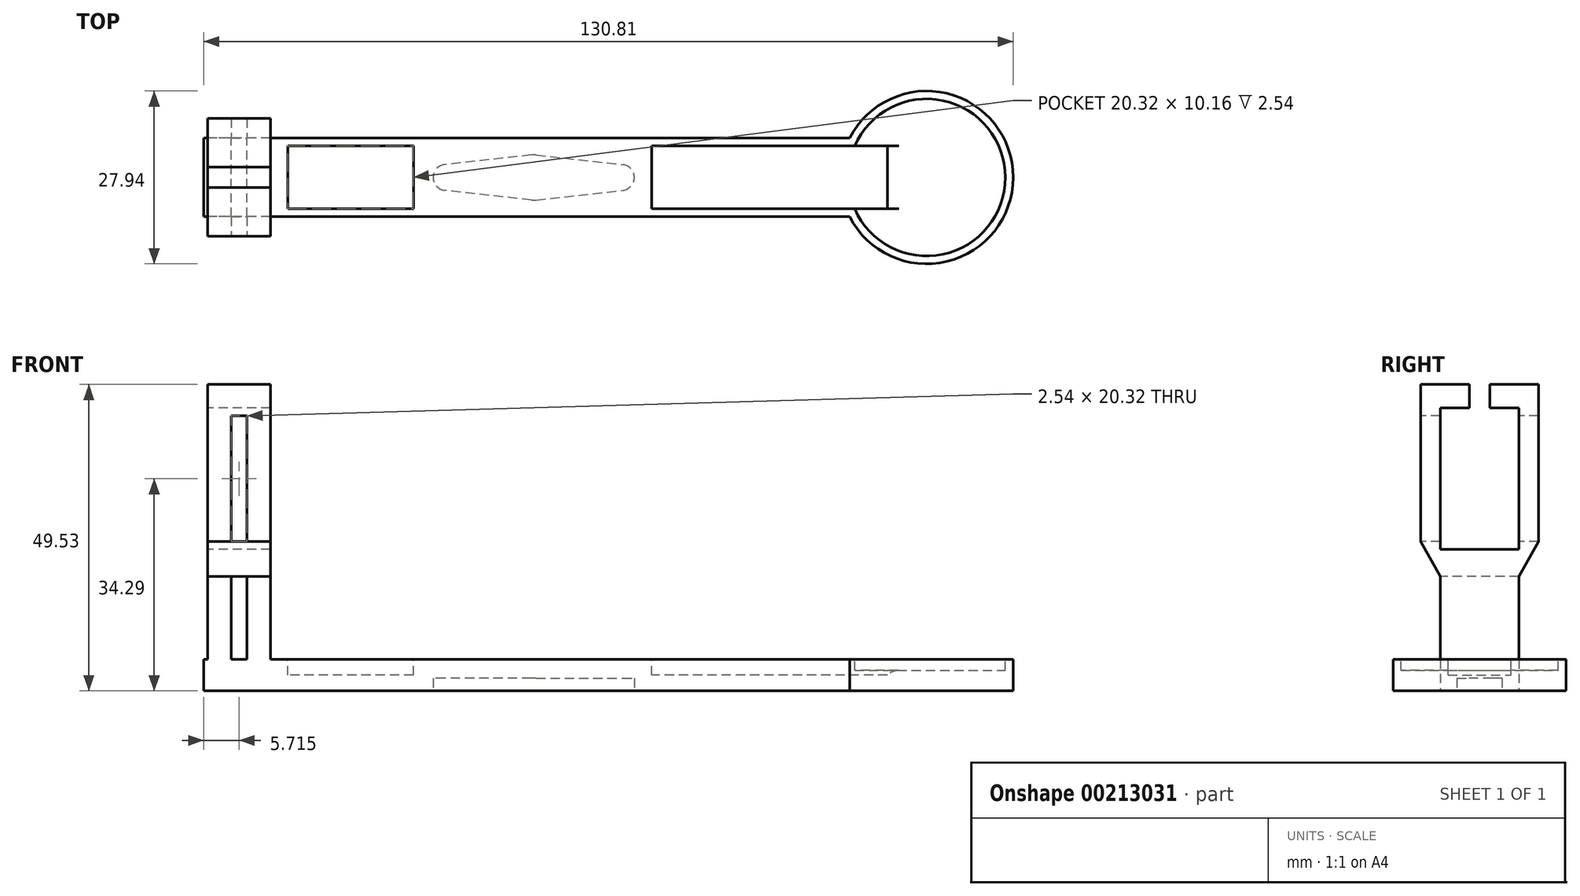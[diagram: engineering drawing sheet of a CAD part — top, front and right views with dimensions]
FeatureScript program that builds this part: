
annotation { "Feature Type Name" : "Feature", "Feature Type Description" : "" }
export const myFeature = defineFeature(function(context is Context, id is Id, definition is map)
    precondition{}
    {
        {
            var Q0;
            Q0=qCreatedBy(makeId("Top.planeOp"),FACE);
            var sketch = newSketch(context, id + "F0", { "sketchPlane" : qUnion([Q0])});
            skPoint(sketch, "E0.middle", {"position": v(0, 0) * mm});
            skLineSegment(sketch, "E1.bottom", {"start": v(-53.34, -6.35) * mm, "end": v(63.5, -6.35) * mm});
            skLineSegment(sketch, "E1.top", {"start": v(-53.34, 6.35) * mm, "end": v(63.5, 6.35) * mm});
            skLineSegment(sketch, "E1.left", {"start": v(-53.34, -6.35) * mm, "end": v(-53.34, 6.35) * mm});
            skLineSegment(sketch, "E1.right", {"start": v(63.5, -6.35) * mm, "end": v(63.5, 6.35) * mm});
            skSolve(sketch);
        }
        {
            var Q0;
            Q0 = qSketchRegion(id + "F0", true);
            extrude(context, id + "F1", {"entities" : qUnion([Q0]), "depth" : 5.08 * mm});
        }
        {
            var Q0;
            Q0=qCreatedBy(makeId("Top.planeOp"),FACE);
            var sketch = newSketch(context, id + "F2", { "sketchPlane" : qUnion([Q0])});
            skCircle(sketch, "E2", {"center": v(63.5, 0) * mm, "radius": 13.97 * mm});
            skSolve(sketch);
        }
        {
            var Q0;
            Q0=makeQuery(id+"F1.opExtrude","CAP_FACE",FACE,{"disambiguationData":[OSD([sQuery(id+"F0.wireOp",EDGE,"E1.bottom"),sQuery(id+"F0.wireOp",EDGE,"E1.top"),sQuery(id+"F0.wireOp",EDGE,"E1.left"),sQuery(id+"F0.wireOp",EDGE,"E1.right")])],"isStart":false});
            var sketch = newSketch(context, id + "F3", { "sketchPlane" : qUnion([Q0])});
            skLineSegment(sketch, "E3.bottom", {"start": v(-42.55, -6.35) * mm, "end": v(-46.35, -6.35) * mm});
            skLineSegment(sketch, "E3.top", {"start": v(-42.55, 6.35) * mm, "end": v(-46.35, 6.35) * mm});
            skLineSegment(sketch, "E3.left", {"start": v(-42.55, -6.35) * mm, "end": v(-42.55, 6.35) * mm});
            skLineSegment(sketch, "E3.right", {"start": v(-46.35, -6.35) * mm, "end": v(-46.35, 6.35) * mm});
            skPoint(sketch, "E3.middle", {"position": v(-44.45, 0) * mm});
            skLineSegment(sketch, "E4.bottom", {"start": v(-48.9, -6.35) * mm, "end": v(-52.7, -6.35) * mm});
            skLineSegment(sketch, "E4.top", {"start": v(-48.9, 6.35) * mm, "end": v(-52.7, 6.35) * mm});
            skLineSegment(sketch, "E4.left", {"start": v(-48.9, -6.35) * mm, "end": v(-48.9, 6.35) * mm});
            skLineSegment(sketch, "E4.right", {"start": v(-52.7, -6.35) * mm, "end": v(-52.7, 6.35) * mm});
            skPoint(sketch, "E4.middle", {"position": v(-50.8, 0) * mm});
            skSolve(sketch);
        }
        {
            var Q0;
            Q0 = qSketchRegion(id + "F3", true);
            extrude(context, id + "F4", {"entities" : qUnion([Q0]), "operationType" : NewBodyOperationType.ADD, "depth" : 40.64 * mm});
        }
        {
            var Q0;
            Q0=makeQuery(id+"F4.opExtrude","SWEPT_FACE",FACE,{"disambiguationData":[OSD([sQuery(id+"F3.wireOp",EDGE,"E4.right")])]});
            var sketch = newSketch(context, id + "F5", { "sketchPlane" : qUnion([Q0])});
            skLineSegment(sketch, "E5", {"start": v(-9.52, 49.53) * mm, "end": v(9.53, 49.53) * mm});
            skLineSegment(sketch, "E6", {"start": v(9.53, 49.53) * mm, "end": v(9.53, 24.13) * mm});
            skLineSegment(sketch, "E7", {"start": v(9.53, 24.13) * mm, "end": v(6.35, 18.54) * mm});
            skLineSegment(sketch, "E8", {"start": v(-6.35, 18.54) * mm, "end": v(-9.52, 24.13) * mm});
            skLineSegment(sketch, "E9", {"start": v(-9.53, 24.13) * mm, "end": v(-9.53, 49.53) * mm});
            skLineSegment(sketch, "E10", {"start": v(-6.35, 18.54) * mm, "end": v(6.35, 18.54) * mm});
            skSolve(sketch);
        }
        {
            var Q0;
            Q0 = qSketchRegion(id + "F5", true);
            var Q1;
            Q1=makeQuery(id+"F4.opExtrude","SWEPT_FACE",FACE,{"disambiguationData":[OSD([sQuery(id+"F3.wireOp",EDGE,"E3.left")])]});
            extrude(context, id + "F6", {"entities" : qUnion([Q0]), "operationType" : NewBodyOperationType.ADD, "endBound" : BoundingType.UP_TO_SURFACE, "oppositeDirection" : true, "endBoundEntityFace" : qUnion([Q1]), "depth" : 25.4 * mm});
        }
        {
            var Q0;
            Q0=makeQuery(id+"F6.boolean.opBoolean","MERGE",FACE,{"derivedFrom":[makeQuery(id+"F4.opExtrude","SWEPT_FACE",FACE,{"disambiguationData":[OSD([sQuery(id+"F3.wireOp",EDGE,"E4.right")])]}),makeQuery(id+"F6.opExtrude","CAP_FACE",FACE,{"disambiguationData":[OSD([sQuery(id+"F5.wireOp",EDGE,"E5"),sQuery(id+"F5.wireOp",EDGE,"E6"),sQuery(id+"F5.wireOp",EDGE,"E7"),sQuery(id+"F5.wireOp",EDGE,"E8"),sQuery(id+"F5.wireOp",EDGE,"E9"),sQuery(id+"F5.wireOp",EDGE,"E10")])],"isStart":true})]});
            var sketch = newSketch(context, id + "F7", { "sketchPlane" : qUnion([Q0])});
            skLineSegment(sketch, "E11.bottom", {"start": v(6.35, 22.86) * mm, "end": v(-6.35, 22.86) * mm});
            skLineSegment(sketch, "E11.top", {"start": v(6.35, 45.72) * mm, "end": v(-6.35, 45.72) * mm});
            skLineSegment(sketch, "E11.left", {"start": v(6.35, 22.86) * mm, "end": v(6.35, 45.72) * mm});
            skLineSegment(sketch, "E11.right", {"start": v(-6.35, 22.86) * mm, "end": v(-6.35, 45.72) * mm});
            skPoint(sketch, "E11.middle", {"position": v(0, 34.3) * mm});
            skSolve(sketch);
        }
        {
            var Q0;
            Q0 = qSketchRegion(id + "F7", true);
            extrude(context, id + "F8", {"entities" : qUnion([Q0]), "operationType" : NewBodyOperationType.REMOVE, "oppositeDirection" : true, "depth" : 25.4 * mm});
        }
        {
            var Q0;
            Q0=makeQuery(id+"F6.opExtrude","SWEPT_FACE",FACE,{"disambiguationData":[OSD([sQuery(id+"F5.wireOp",EDGE,"E6")])]});
            var sketch = newSketch(context, id + "F9", { "sketchPlane" : qUnion([Q0])});
            skLineSegment(sketch, "E12.bottom", {"start": v(-46.35, 24.13) * mm, "end": v(-48.9, 24.13) * mm});
            skLineSegment(sketch, "E12.top", {"start": v(-46.35, 44.45) * mm, "end": v(-48.9, 44.45) * mm});
            skLineSegment(sketch, "E12.left", {"start": v(-46.35, 24.13) * mm, "end": v(-46.35, 44.45) * mm});
            skLineSegment(sketch, "E12.right", {"start": v(-48.9, 24.13) * mm, "end": v(-48.9, 44.45) * mm});
            skPoint(sketch, "E12.middle", {"position": v(-47.62, 34.3) * mm});
            skPoint(sketch, "E12.middle.positionSnap0", {"position": v(-47.62, 24.13) * mm});
            skPoint(sketch, "E12.centerSnap0", {"position": v(-47.62, 24.13) * mm});
            skSolve(sketch);
        }
        {
            var Q0;
            Q0 = qSketchRegion(id + "F9", true);
            extrude(context, id + "F10", {"entities" : qUnion([Q0]), "operationType" : NewBodyOperationType.REMOVE, "oppositeDirection" : true, "depth" : 25.4 * mm});
        }
        {
            var Q0;
            {var subQ0=sQuery(id+"F3.wireOp",EDGE,"E3.left");Q0=makeQuery(id+"F6.boolean.opBoolean","MERGE",FACE,{"derivedFrom":[makeQuery(id+"F4.opExtrude","SWEPT_FACE",FACE,{"disambiguationData":[OSD([subQ0])]}),makeQuery(id+"F6.opExtrude","CAP_FACE",FACE,{"disambiguationData":[OSD([subQ0])],"isStart":false})]});}
            var sketch = newSketch(context, id + "F11", { "sketchPlane" : qUnion([Q0])});
            skLineSegment(sketch, "E13.bottom", {"start": v(1.65, 42.81) * mm, "end": v(-1.65, 42.81) * mm});
            skLineSegment(sketch, "E13.top", {"start": v(1.65, 52.44) * mm, "end": v(-1.65, 52.44) * mm});
            skLineSegment(sketch, "E13.left", {"start": v(1.65, 42.81) * mm, "end": v(1.65, 52.44) * mm});
            skLineSegment(sketch, "E13.right", {"start": v(-1.65, 42.81) * mm, "end": v(-1.65, 52.44) * mm});
            skPoint(sketch, "E13.middle", {"position": v(0, 47.63) * mm});
            skSolve(sketch);
        }
        {
            var Q0;
            Q0 = qSketchRegion(id + "F11", true);
            extrude(context, id + "F12", {"entities" : qUnion([Q0]), "operationType" : NewBodyOperationType.REMOVE, "oppositeDirection" : true, "depth" : 25.4 * mm});
        }
        {
            var Q0;
            Q0 = qSketchRegion(id + "F2", true);
            extrude(context, id + "F13", {"entities" : qUnion([Q0]), "operationType" : NewBodyOperationType.ADD, "depth" : 5.08 * mm});
        }
        {
            var Q0;
            {var subQ0=sQuery(id+"F0.wireOp",EDGE,"E1.right");var subQ1=sQuery(id+"F0.wireOp",EDGE,"E1.top");var subQ2=sQuery(id+"F0.wireOp",EDGE,"E1.bottom");Q0=makeQuery(id+"F13.boolean.opBoolean","MERGE",FACE,{"derivedFrom":[makeQuery(id+"F4.boolean.opBoolean","SPLIT",FACE,{"disambiguationData":[TD([makeQuery(id+"F1.opExtrude","SWEPT_FACE",FACE,{"disambiguationData":[OSD([subQ0])]})])],"derivedFrom":makeQuery(id+"F1.opExtrude","CAP_FACE",FACE,{"disambiguationData":[OSD([subQ2,subQ1,sQuery(id+"F0.wireOp",EDGE,"E1.left"),subQ0])],"isStart":false})}),makeQuery(id+"F13.opExtrude","CAP_FACE",FACE,{"disambiguationData":[OSD([sQuery(id+"F2.wireOp",EDGE,"E2")])],"isStart":false})]});}
            var sketch = newSketch(context, id + "F14", { "sketchPlane" : qUnion([Q0])});
            skCircle(sketch, "E14", {"center": v(63.5, 0) * mm, "radius": 12.7 * mm});
            skSolve(sketch);
        }
        {
            var Q0;
            Q0 = qSketchRegion(id + "F14", true);
            extrude(context, id + "F15", {"entities" : qUnion([Q0]), "operationType" : NewBodyOperationType.REMOVE, "oppositeDirection" : true, "depth" : 1.78 * mm});
        }
        {
            var Q0;
            Q0=makeQuery(id+"F13.boolean.opBoolean","MERGE",FACE,{"derivedFrom":[makeQuery(id+"F1.opExtrude","CAP_FACE",FACE,{"disambiguationData":[OSD([sQuery(id+"F0.wireOp",EDGE,"E1.bottom"),sQuery(id+"F0.wireOp",EDGE,"E1.top"),sQuery(id+"F0.wireOp",EDGE,"E1.left"),sQuery(id+"F0.wireOp",EDGE,"E1.right")])],"isStart":true}),makeQuery(id+"F13.opExtrude","CAP_FACE",FACE,{"disambiguationData":[OSD([sQuery(id+"F2.wireOp",EDGE,"E2")])],"isStart":true})]});
            var sketch = newSketch(context, id + "F16", { "sketchPlane" : qUnion([Q0])});
            skArc(sketch, "E15", {"start": v(-0.4, -3.64) * mm, "mid": v(0, -3.66) * mm, "end": v(0.4, -3.64) * mm});
            skLineSegment(sketch, "E16.bottom", {"start": v(14.16, -2.1) * mm, "end": v(-14.16, -2.1) * mm, "construction": true});
            skLineSegment(sketch, "E16.top", {"start": v(14.16, 2.1) * mm, "end": v(-14.16, 2.1) * mm, "construction": true});
            skLineSegment(sketch, "E16.left", {"start": v(16.26, 0) * mm, "end": v(16.26, 0) * mm});
            skLineSegment(sketch, "E16.right", {"start": v(-16.26, 0) * mm, "end": v(-16.26, 0) * mm});
            skPoint(sketch, "E17.visualSharp", {"position": v(16.26, 2.1) * mm});
            skArc(sketch, "E17.filletArc", {"start": v(16.26, 0) * mm, "mid": v(15.64, 1.48) * mm, "end": v(14.16, 2.1) * mm});
            skPoint(sketch, "E18.visualSharp", {"position": v(16.26, -2.1) * mm});
            skArc(sketch, "E18.filletArc", {"start": v(14.16, -2.1) * mm, "mid": v(15.64, -1.48) * mm, "end": v(16.26, 0) * mm});
            skPoint(sketch, "E19.visualSharp", {"position": v(-16.26, 2.1) * mm});
            skArc(sketch, "E19.filletArc", {"start": v(-14.16, 2.1) * mm, "mid": v(-15.64, 1.48) * mm, "end": v(-16.26, 0) * mm});
            skPoint(sketch, "E20.visualSharp", {"position": v(-16.26, -2.1) * mm});
            skArc(sketch, "E20.filletArc", {"start": v(-16.26, 0) * mm, "mid": v(-15.64, -1.48) * mm, "end": v(-14.16, -2.1) * mm});
            skLineSegment(sketch, "E21", {"start": v(0.4, 3.64) * mm, "end": v(14.4, 2.08) * mm});
            skLineSegment(sketch, "E22.MirrorCS", {"start": v(-0.4, 3.64) * mm, "end": v(-14.4, 2.08) * mm});
            skLineSegment(sketch, "E23.MirrorCS", {"start": v(-0.4, -3.64) * mm, "end": v(-14.4, -2.08) * mm});
            skLineSegment(sketch, "E24.MirrorCS", {"start": v(0.4, -3.64) * mm, "end": v(14.4, -2.08) * mm});
            skArc(sketch, "E25.trimOffspring", {"start": v(0.4, 3.64) * mm, "mid": v(0, 3.66) * mm, "end": v(-0.4, 3.64) * mm});
            skSolve(sketch);
        }
        {
            var Q0;
            Q0 = qSketchRegion(id + "F16", true);
            extrude(context, id + "F17", {"entities" : qUnion([Q0]), "operationType" : NewBodyOperationType.REMOVE, "oppositeDirection" : true, "depth" : 2.03 * mm});
        }
        {
            var Q0;
            {var subQ0=sQuery(id+"F0.wireOp",EDGE,"E1.right");var subQ1=sQuery(id+"F0.wireOp",EDGE,"E1.top");var subQ2=sQuery(id+"F0.wireOp",EDGE,"E1.bottom");Q0=makeQuery(id+"F13.boolean.opBoolean","MERGE",FACE,{"derivedFrom":[makeQuery(id+"F4.boolean.opBoolean","SPLIT",FACE,{"disambiguationData":[TD([makeQuery(id+"F1.opExtrude","SWEPT_FACE",FACE,{"disambiguationData":[OSD([subQ0])]})])],"derivedFrom":makeQuery(id+"F1.opExtrude","CAP_FACE",FACE,{"disambiguationData":[OSD([subQ2,subQ1,sQuery(id+"F0.wireOp",EDGE,"E1.left"),subQ0])],"isStart":false})}),makeQuery(id+"F13.opExtrude","CAP_FACE",FACE,{"disambiguationData":[OSD([sQuery(id+"F2.wireOp",EDGE,"E2")])],"isStart":false})]});}
            var sketch = newSketch(context, id + "F18", { "sketchPlane" : qUnion([Q0])});
            skLineSegment(sketch, "E26.bottom", {"start": v(-19.46, -5.08) * mm, "end": v(-39.78, -5.08) * mm});
            skLineSegment(sketch, "E26.top", {"start": v(-19.46, 5.08) * mm, "end": v(-39.78, 5.08) * mm});
            skLineSegment(sketch, "E26.left", {"start": v(-19.46, -5.08) * mm, "end": v(-19.46, 5.08) * mm});
            skLineSegment(sketch, "E26.right", {"start": v(-39.78, -5.08) * mm, "end": v(-39.78, 5.08) * mm});
            skPoint(sketch, "E26.middle", {"position": v(-29.62, 0) * mm});
            skLineSegment(sketch, "E27.bottom", {"start": v(57.15, -5.08) * mm, "end": v(19.05, -5.08) * mm});
            skLineSegment(sketch, "E27.top", {"start": v(57.15, 5.08) * mm, "end": v(19.05, 5.08) * mm});
            skLineSegment(sketch, "E27.left", {"start": v(57.15, -5.08) * mm, "end": v(57.15, 5.08) * mm});
            skLineSegment(sketch, "E27.right", {"start": v(19.05, -5.08) * mm, "end": v(19.05, 5.08) * mm});
            skPoint(sketch, "E27.middle", {"position": v(38.1, 0) * mm});
            skSolve(sketch);
        }
        {
            var Q0;
            Q0 = qSketchRegion(id + "F18", true);
            extrude(context, id + "F19", {"entities" : qUnion([Q0]), "operationType" : NewBodyOperationType.REMOVE, "oppositeDirection" : true, "depth" : 2.54 * mm});
        }
        {
            var Q0;
            Q0=makeQuery(id+"F19.boolean.opBoolean","COPY",EDGE,{"derivedFrom":makeQuery(id+"F19.opExtrude","CAP_EDGE",EDGE,{"disambiguationData":[OSD([sQuery(id+"F18.wireOp",EDGE,"E26.right")])],"isStart":true})});
            var Q1;
            Q1=makeQuery(id+"F19.boolean.opBoolean","COPY",EDGE,{"derivedFrom":makeQuery(id+"F19.opExtrude","CAP_EDGE",EDGE,{"disambiguationData":[OSD([sQuery(id+"F18.wireOp",EDGE,"E26.left")])],"isStart":true})});
            var Q2;
            Q2=makeQuery(id+"F19.boolean.opBoolean","COPY",EDGE,{"derivedFrom":makeQuery(id+"F19.opExtrude","CAP_EDGE",EDGE,{"disambiguationData":[OSD([sQuery(id+"F18.wireOp",EDGE,"E27.right")])],"isStart":true})});
            var Q3;
            Q3=makeQuery(id+"F19.boolean.opBoolean","INTERSECT",EDGE,{"derivedFrom":[makeQuery(id+"F15.boolean.opBoolean","COPY",FACE,{"derivedFrom":makeQuery(id+"F15.opExtrude","CAP_FACE",FACE,{"disambiguationData":[OSD([sQuery(id+"F14.wireOp",EDGE,"E14")])],"isStart":false})}),makeQuery(id+"F19.opExtrude","SWEPT_FACE",FACE,{"disambiguationData":[OSD([sQuery(id+"F18.wireOp",EDGE,"E27.left")])]})]});
            fillet(context, id + "F20", {"entities" : qUnion([Q0, Q1, Q2, Q3]), "radius" : 2.54 * mm, "tangentPropagation" : true, "allowEdgeOverflow" : false});
        }
    });
